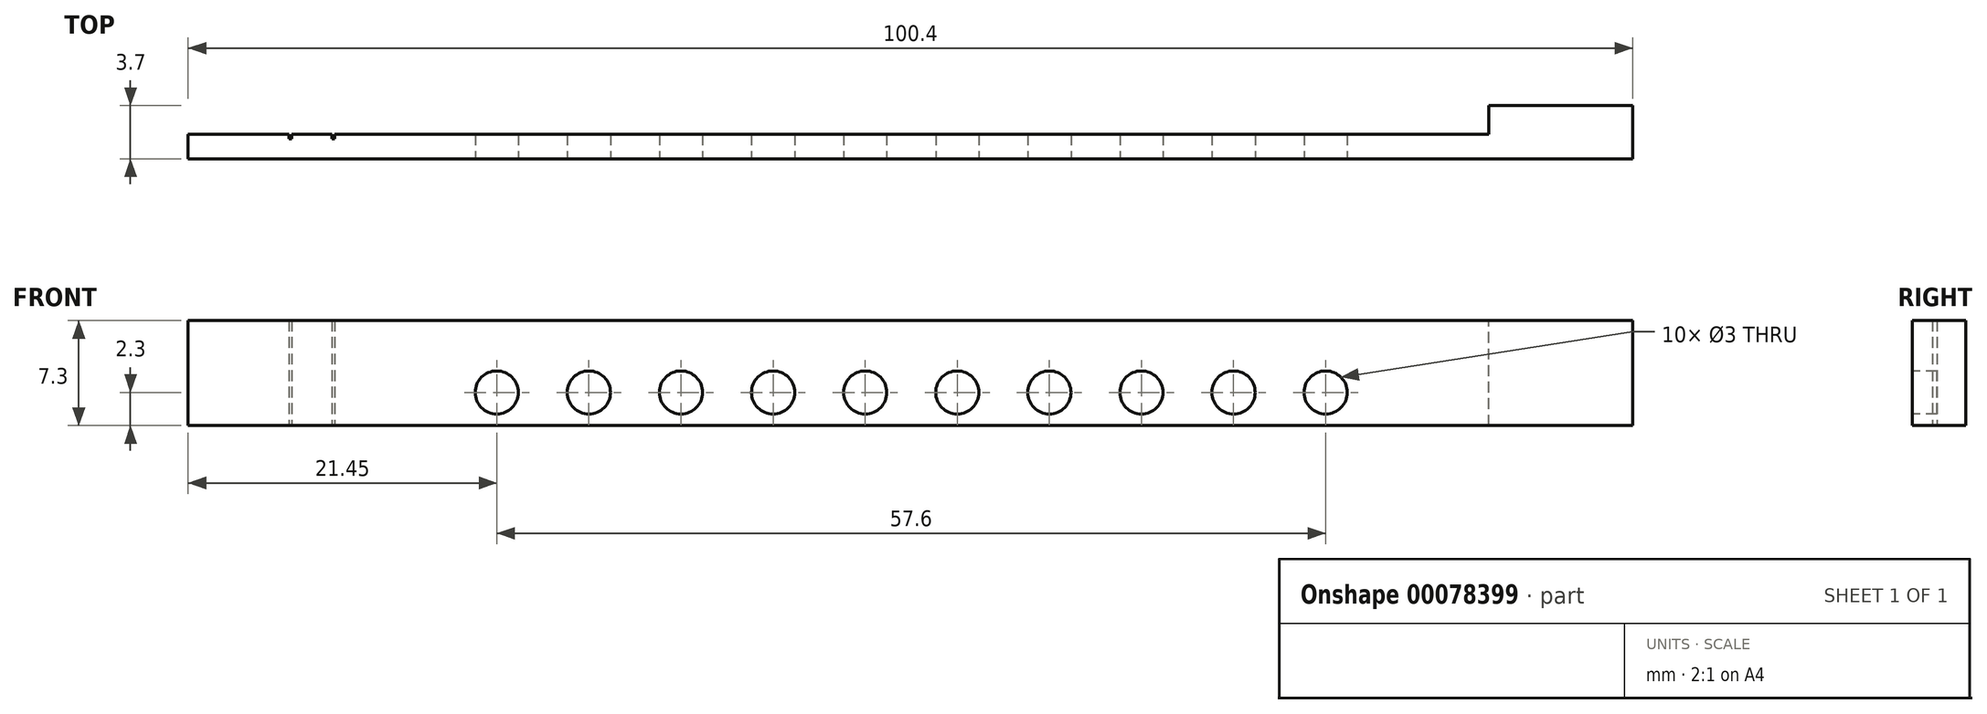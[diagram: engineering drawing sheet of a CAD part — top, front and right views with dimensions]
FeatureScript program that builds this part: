
annotation { "Feature Type Name" : "Feature", "Feature Type Description" : "" }
export const myFeature = defineFeature(function(context is Context, id is Id, definition is map)
    precondition{}
    {
        {
            var Q0;
            Q0=qCreatedBy(makeId("Front.planeOp"),FACE);
            var sketch = newSketch(context, id + "F0", { "sketchPlane" : qUnion([Q0])});
            skLineSegment(sketch, "E0.bottom", {"start": v(-50.2, 3.65) * mm, "end": v(50.2, 3.65) * mm});
            skLineSegment(sketch, "E0.top", {"start": v(-50.2, -3.65) * mm, "end": v(50.2, -3.65) * mm});
            skLineSegment(sketch, "E0.left", {"start": v(-50.2, 3.65) * mm, "end": v(-50.2, -3.65) * mm});
            skLineSegment(sketch, "E0.right", {"start": v(50.2, 3.65) * mm, "end": v(50.2, -3.65) * mm});
            skPoint(sketch, "E0.middle", {"position": v(0, 0) * mm});
            skSolve(sketch);
        }
        {
            var Q0;
            Q0=makeQuery(id+"F0.imprint","IMPRINT",FACE,{"disambiguationData":[TD([[makeQuery(id+"F0.imprint","IMPRINT",EDGE,{"derivedFrom":sQuery(id+"F0.wireOp",EDGE,"E0.bottom")}),-1.0]])]});
            extrude(context, id + "F1", {"entities" : qUnion([Q0]), "depth" : 1.7 * mm, "offsetDistance" : 25 * mm});
        }
        {
            var Q0;
            Q0=makeQuery(id+"F1.opExtrude","CAP_FACE",FACE,{"disambiguationData":[OSD([sQuery(id+"F0.wireOp",EDGE,"E0.bottom"),sQuery(id+"F0.wireOp",EDGE,"E0.top"),sQuery(id+"F0.wireOp",EDGE,"E0.left"),sQuery(id+"F0.wireOp",EDGE,"E0.right")])],"isStart":false});
            var sketch = newSketch(context, id + "F2", { "sketchPlane" : qUnion([Q0])});
            skCircle(sketch, "E1", {"center": v(-28.75, -1.35) * mm, "radius": 1.5 * mm});
            skCircle(sketch, "E2.1.0.0", {"center": v(-22.35, -1.35) * mm, "radius": 1.5 * mm});
            skCircle(sketch, "E2.2.0.0", {"center": v(-15.95, -1.35) * mm, "radius": 1.5 * mm});
            skCircle(sketch, "E2.3.0.0", {"center": v(-9.55, -1.35) * mm, "radius": 1.5 * mm});
            skCircle(sketch, "E2.4.0.0", {"center": v(-3.15, -1.35) * mm, "radius": 1.5 * mm});
            skCircle(sketch, "E2.5.0.0", {"center": v(3.25, -1.35) * mm, "radius": 1.5 * mm});
            skCircle(sketch, "E2.6.0.0", {"center": v(9.65, -1.35) * mm, "radius": 1.5 * mm});
            skCircle(sketch, "E2.7.0.0", {"center": v(16.05, -1.35) * mm, "radius": 1.5 * mm});
            skCircle(sketch, "E2.8.0.0", {"center": v(22.45, -1.35) * mm, "radius": 1.5 * mm});
            skCircle(sketch, "E2.9.0.0", {"center": v(28.85, -1.35) * mm, "radius": 1.5 * mm});
            skLineSegment(sketch, "E2.direction1", {"start": v(-28.75, -1.35) * mm, "end": v(-22.35, -1.35) * mm, "construction": true});
            skSolve(sketch);
        }
        {
            var Q0;
            Q0=makeQuery(id+"F2.imprint","IMPRINT",FACE,{"disambiguationData":[TD([[makeQuery(id+"F2.imprint","IMPRINT",EDGE,{"derivedFrom":sQuery(id+"F2.wireOp",EDGE,"E1")}),1.0]])]});
            var Q1;
            Q1=makeQuery(id+"F2.imprint","IMPRINT",FACE,{"disambiguationData":[TD([[makeQuery(id+"F2.imprint","IMPRINT",EDGE,{"derivedFrom":sQuery(id+"F2.wireOp",EDGE,"E2.1.0.0")}),1.0]])]});
            var Q2;
            Q2=makeQuery(id+"F2.imprint","IMPRINT",FACE,{"disambiguationData":[TD([[makeQuery(id+"F2.imprint","IMPRINT",EDGE,{"derivedFrom":sQuery(id+"F2.wireOp",EDGE,"E2.2.0.0")}),1.0]])]});
            var Q3;
            Q3=makeQuery(id+"F2.imprint","IMPRINT",FACE,{"disambiguationData":[TD([[makeQuery(id+"F2.imprint","IMPRINT",EDGE,{"derivedFrom":sQuery(id+"F2.wireOp",EDGE,"E2.3.0.0")}),1.0]])]});
            var Q4;
            Q4=makeQuery(id+"F2.imprint","IMPRINT",FACE,{"disambiguationData":[TD([[makeQuery(id+"F2.imprint","IMPRINT",EDGE,{"derivedFrom":sQuery(id+"F2.wireOp",EDGE,"E2.4.0.0")}),1.0]])]});
            var Q5;
            Q5=makeQuery(id+"F2.imprint","IMPRINT",FACE,{"disambiguationData":[TD([[makeQuery(id+"F2.imprint","IMPRINT",EDGE,{"derivedFrom":sQuery(id+"F2.wireOp",EDGE,"E2.5.0.0")}),1.0]])]});
            var Q6;
            Q6=makeQuery(id+"F2.imprint","IMPRINT",FACE,{"disambiguationData":[TD([[makeQuery(id+"F2.imprint","IMPRINT",EDGE,{"derivedFrom":sQuery(id+"F2.wireOp",EDGE,"E2.6.0.0")}),1.0]])]});
            var Q7;
            Q7=makeQuery(id+"F2.imprint","IMPRINT",FACE,{"disambiguationData":[TD([[makeQuery(id+"F2.imprint","IMPRINT",EDGE,{"derivedFrom":sQuery(id+"F2.wireOp",EDGE,"E2.7.0.0")}),1.0]])]});
            var Q8;
            Q8=makeQuery(id+"F2.imprint","IMPRINT",FACE,{"disambiguationData":[TD([[makeQuery(id+"F2.imprint","IMPRINT",EDGE,{"derivedFrom":sQuery(id+"F2.wireOp",EDGE,"E2.8.0.0")}),1.0]])]});
            var Q9;
            Q9=makeQuery(id+"F2.imprint","IMPRINT",FACE,{"disambiguationData":[TD([[makeQuery(id+"F2.imprint","IMPRINT",EDGE,{"derivedFrom":sQuery(id+"F2.wireOp",EDGE,"E2.9.0.0")}),1.0]])]});
            extrude(context, id + "F3", {"entities" : qUnion([Q0, Q1, Q2, Q3, Q4, Q5, Q6, Q7, Q8, Q9]), "operationType" : NewBodyOperationType.REMOVE, "endBound" : BoundingType.THROUGH_ALL, "oppositeDirection" : true, "depth" : 25 * mm, "offsetDistance" : 25 * mm});
        }
        {
            var Q0;
            Q0=makeQuery(id+"F1.opExtrude","CAP_FACE",FACE,{"disambiguationData":[OSD([sQuery(id+"F0.wireOp",EDGE,"E0.bottom"),sQuery(id+"F0.wireOp",EDGE,"E0.top"),sQuery(id+"F0.wireOp",EDGE,"E0.left"),sQuery(id+"F0.wireOp",EDGE,"E0.right")])],"isStart":true});
            var sketch = newSketch(context, id + "F4", { "sketchPlane" : qUnion([Q0])});
            skLineSegment(sketch, "E3.bottom", {"start": v(-50.2, -3.65) * mm, "end": v(-40.2, -3.65) * mm});
            skLineSegment(sketch, "E3.top", {"start": v(-50.2, 3.65) * mm, "end": v(-40.2, 3.65) * mm});
            skLineSegment(sketch, "E3.left", {"start": v(-50.2, -3.65) * mm, "end": v(-50.2, 3.65) * mm});
            skLineSegment(sketch, "E3.right", {"start": v(-40.2, -3.65) * mm, "end": v(-40.2, 3.65) * mm});
            skSolve(sketch);
        }
        {
            var Q0;
            Q0=makeQuery(id+"F4.imprint","IMPRINT",FACE,{"disambiguationData":[TD([[makeQuery(id+"F4.imprint","IMPRINT",EDGE,{"derivedFrom":sQuery(id+"F4.wireOp",EDGE,"E3.bottom")}),-1.0]])]});
            extrude(context, id + "F5", {"entities" : qUnion([Q0]), "operationType" : NewBodyOperationType.ADD, "depth" : 2 * mm, "offsetDistance" : 25 * mm});
        }
        {
            var Q0;
            Q0=makeQuery(id+"F1.opExtrude","CAP_FACE",FACE,{"disambiguationData":[OSD([sQuery(id+"F0.wireOp",EDGE,"E0.bottom"),sQuery(id+"F0.wireOp",EDGE,"E0.top"),sQuery(id+"F0.wireOp",EDGE,"E0.left"),sQuery(id+"F0.wireOp",EDGE,"E0.right")])],"isStart":true});
            var sketch = newSketch(context, id + "F6", { "sketchPlane" : qUnion([Q0])});
            skLineSegment(sketch, "E4.bottom", {"start": v(50.2, -3.65) * mm, "end": v(43.2, -3.65) * mm});
            skLineSegment(sketch, "E4.top", {"start": v(50.2, 3.65) * mm, "end": v(43.2, 3.65) * mm});
            skLineSegment(sketch, "E4.left", {"start": v(50.2, -3.65) * mm, "end": v(50.2, 3.65) * mm});
            skLineSegment(sketch, "E4.right", {"start": v(43.2, -3.65) * mm, "end": v(43.2, 3.65) * mm});
            skSolve(sketch);
        }
        {
            var Q0;
            Q0=makeQuery(id+"F1.opExtrude","CAP_FACE",FACE,{"disambiguationData":[OSD([sQuery(id+"F0.wireOp",EDGE,"E0.bottom"),sQuery(id+"F0.wireOp",EDGE,"E0.top"),sQuery(id+"F0.wireOp",EDGE,"E0.left"),sQuery(id+"F0.wireOp",EDGE,"E0.right")])],"isStart":true});
            var sketch = newSketch(context, id + "F7", { "sketchPlane" : qUnion([Q0])});
            skLineSegment(sketch, "E5.bottom", {"start": v(40, 3.65) * mm, "end": v(40.2, 3.65) * mm});
            skLineSegment(sketch, "E5.top", {"start": v(40, -3.65) * mm, "end": v(40.2, -3.65) * mm});
            skLineSegment(sketch, "E5.left", {"start": v(40, 3.65) * mm, "end": v(40, -3.65) * mm});
            skLineSegment(sketch, "E5.right", {"start": v(40.2, 3.65) * mm, "end": v(40.2, -3.65) * mm});
            skSolve(sketch);
        }
        {
            var Q0;
            Q0=makeQuery(id+"F7.imprint","IMPRINT",FACE,{"disambiguationData":[TD([[makeQuery(id+"F7.imprint","IMPRINT",EDGE,{"derivedFrom":sQuery(id+"F7.wireOp",EDGE,"E5.bottom")}),1.0]])]});
            extrude(context, id + "F8", {"entities" : qUnion([Q0]), "operationType" : NewBodyOperationType.REMOVE, "oppositeDirection" : true, "depth" : 0.3 * mm, "offsetDistance" : 25 * mm});
        }
        {
            var Q0;
            {var subQ0=sQuery(id+"F0.wireOp",EDGE,"E0.left");var subQ1=sQuery(id+"F0.wireOp",EDGE,"E0.top");var subQ2=sQuery(id+"F0.wireOp",EDGE,"E0.bottom");Q0=makeQuery(id+"F8.boolean.opBoolean","SPLIT",FACE,{"disambiguationData":[TD([makeQuery(id+"F1.opExtrude","SWEPT_FACE",FACE,{"disambiguationData":[OSD([subQ0])]})])],"derivedFrom":makeQuery(id+"F1.opExtrude","CAP_FACE",FACE,{"disambiguationData":[OSD([subQ2,subQ1,subQ0,sQuery(id+"F0.wireOp",EDGE,"E0.right")])],"isStart":true})});}
            var sketch = newSketch(context, id + "F9", { "sketchPlane" : qUnion([Q0])});
            skLineSegment(sketch, "E6.bottom", {"start": v(43, 3.65) * mm, "end": v(43.2, 3.65) * mm});
            skLineSegment(sketch, "E6.top", {"start": v(43, -3.65) * mm, "end": v(43.2, -3.65) * mm});
            skLineSegment(sketch, "E6.left", {"start": v(43, 3.65) * mm, "end": v(43, -3.65) * mm});
            skLineSegment(sketch, "E6.right", {"start": v(43.2, 3.65) * mm, "end": v(43.2, -3.65) * mm});
            skSolve(sketch);
        }
        {
            var Q0;
            Q0=makeQuery(id+"F9.imprint","IMPRINT",FACE,{"disambiguationData":[TD([[makeQuery(id+"F9.imprint","IMPRINT",EDGE,{"derivedFrom":sQuery(id+"F9.wireOp",EDGE,"E6.bottom")}),1.0]])]});
            extrude(context, id + "F10", {"entities" : qUnion([Q0]), "operationType" : NewBodyOperationType.REMOVE, "oppositeDirection" : true, "depth" : 0.3 * mm, "offsetDistance" : 25 * mm});
        }
    });
